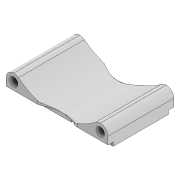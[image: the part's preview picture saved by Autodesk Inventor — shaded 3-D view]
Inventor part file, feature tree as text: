
AUTODESK INVENTOR PART (.ipt)
format: ipt  version: 2020 (Build 240168000, 168)  size: 343,552 bytes
history: native  units: mm
features: extrude x11, sketch x10, fillet x7, projected_geometry x7, mirror x2, plane x1
ambient origin geometry x8: Origin, YZ Plane, XZ Plane, XY Plane, X Axis, Y Axis, Z Axis, Center Point
bodies: Solid1 (feature_tree)
feature tree (38):
  extrude  "Extrusion1"  Depth=6.0mm
  extrude  "Extrusion2"  Depth=3.0mm
  extrude  "Extrusion3"  Depth=3.0mm
  mirror  "Mirror1"
  extrude  "Extrusion4"  Depth=10.0mm TaperAngle=0.0deg
  extrude  "Extrusion5"  Depth=2.05mm TaperAngle=0.0deg
  fillet  "Fillet1"  [1 undecoded]
  plane  "Work Plane1"
  mirror  "Mirror2"
  extrude  "Extrusion7"  Depth=3.0mm
  extrude  "Extrusion8"  TaperAngle=0.0deg  [1 undecoded]
  fillet  "Fillet2"  Radius=500.0mm
  fillet  "Fillet3"  Radius=17.1mm
  sketch  "Sketch9"  dims[d25=1.5mm d26=10.0mm d27=0.0mm]
  extrude  "Extrusion9"  Depth=10.0mm TaperAngle=0.0deg
  extrude  "Extrusion10"  Depth=1.5mm TaperAngle=0.0deg
  fillet  "Fillet4"  Radius=1.5mm
  extrude  "Extrusion11"  Depth=3.5mm
  extrude  "Extrusion12"  Depth=3.5mm
  fillet  "Fillet5"  Radius=3.0mm
  fillet  "Fillet7"  Radius=10.0mm
  fillet  "Fillet8"  [1 undecoded]
  sketch  "Sketch1"  dims[d0=3.4mm d1=6.0mm]
  sketch  "Sketch2"  dims[d2=26.0mm d3=0.0mm d4=3.0mm]
  sketch  "Sketch3"  dims[d5=8.0mm d6=3.0mm]
  sketch  "Sketch4"  dims[d7=5.0mm d8=10.0mm d9=0.0mm]
  sketch  "Sketch5"  dims[d10=5.0mm d11=2.05mm d12=0.0mm d14=0.0mm d15=0.0mm]
  sketch  "Sketch7"  dims[d16=1.5mm d17=3.0mm]
  projected_geometry  "Projected Loop2"
  sketch  "Sketch8"  dims[d18=3.0mm d19=0.0mm d20=0.0mm d21=500.0mm d24=17.1mm]
  projected_geometry  "Projected Loop3"
  projected_geometry  "Projected Loop4"
  sketch  "Sketch10"  dims[d28=11.537mm d29=1.5mm d30=0.0mm d31=1.5mm]
  projected_geometry  "Projected Loop5"
  sketch  "Sketch11"  dims[d32=1.5mm d33=1.1mm d34=1.1mm d35=3.0mm d36=10.0mm d37=0.0mm d38=0.0mm d39=0.0mm d40=3.0mm d43=10.0mm d44=0.0mm d47=10.0mm d48=10.0mm d49=0.0mm d50=26.0mm d51=5.0mm d52=0.0mm d53=0.0mm d54=3.0mm d56=10.0mm d57=180.0deg d58=3.5mm d59=9.0mm d60=3.5mm d61=8.0mm d62=0.0mm d63=3.5mm d64=9.0mm d65=3.5mm]
  projected_geometry  "Projected Loop6"
  projected_geometry  "Projected Loop7"
  projected_geometry  "Projected Loop8"
note: 3 required parameter values undecoded (feature->parameter linkage not recoverable at this tier; creation-order binding heuristic only, values carry confidence <= 0.55)
